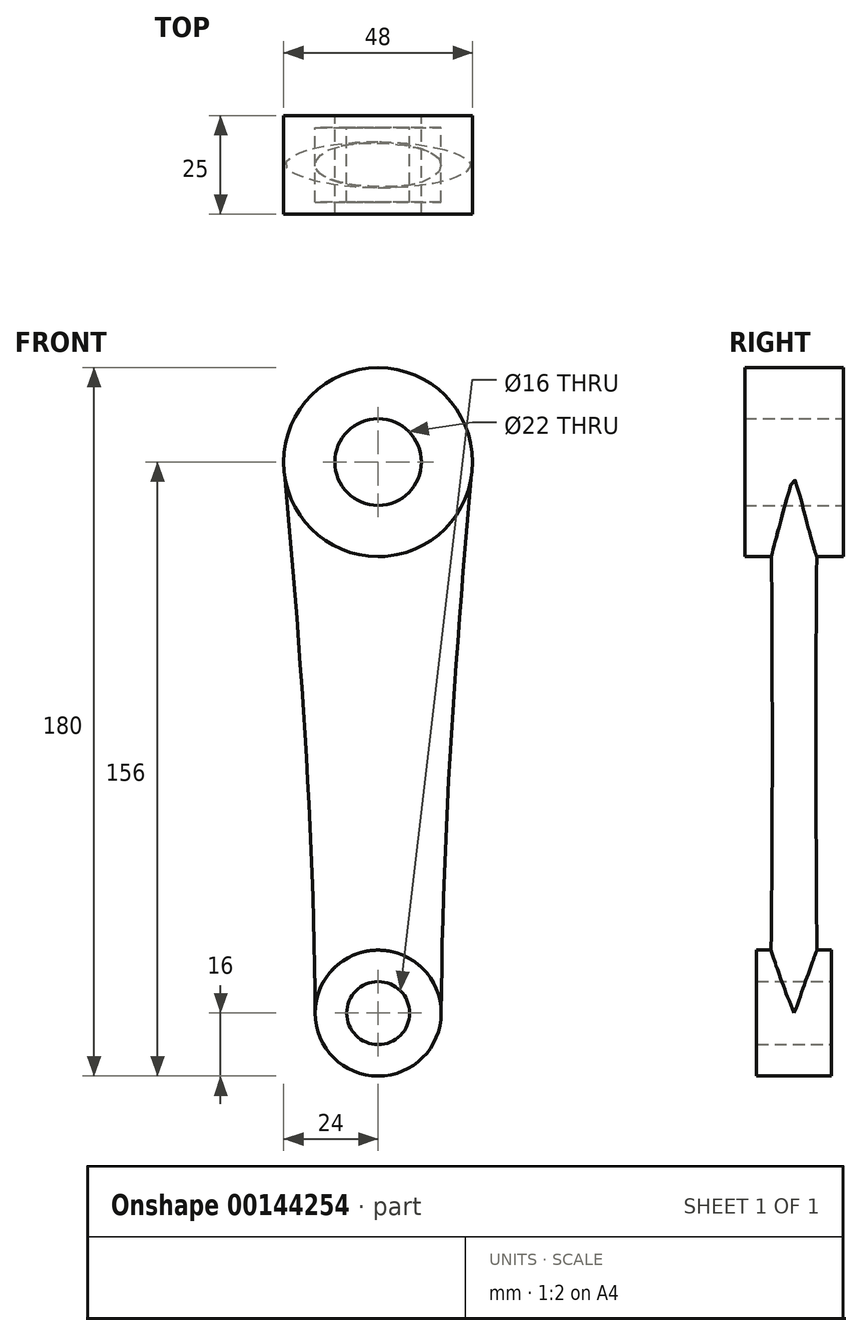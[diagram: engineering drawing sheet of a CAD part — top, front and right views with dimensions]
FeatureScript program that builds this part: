
annotation { "Feature Type Name" : "Feature", "Feature Type Description" : "" }
export const myFeature = defineFeature(function(context is Context, id is Id, definition is map)
    precondition{}
    {
        {
            var Q0;
            Q0=qCreatedBy(makeId("Front.planeOp"),FACE);
            var sketch = newSketch(context, id + "F0", { "sketchPlane" : qUnion([Q0])});
            skCircle(sketch, "E0", {"center": v(0, 140) * mm, "radius": 11 * mm});
            skCircle(sketch, "E1", {"center": v(0, 140) * mm, "radius": 24 * mm});
            skCircle(sketch, "E2", {"center": v(0, 0) * mm, "radius": 8 * mm});
            skCircle(sketch, "E3", {"center": v(0, 0) * mm, "radius": 16 * mm});
            skLineSegment(sketch, "E4", {"start": v(0, 0) * mm, "end": v(0, 140) * mm, "construction": true});
            skSolve(sketch);
        }
        {
            var Q0;
            Q0=makeQuery(id+"F0.imprint","IMPRINT",FACE,{"disambiguationData":[TD([[makeQuery(id+"F0.imprint","IMPRINT",EDGE,{"derivedFrom":sQuery(id+"F0.wireOp",EDGE,"E0")}),-1.0]])]});
            var Q1;
            Q1=makeQuery(id+"F0.imprint","IMPRINT",FACE,{"disambiguationData":[TD([[makeQuery(id+"F0.imprint","IMPRINT",EDGE,{"derivedFrom":sQuery(id+"F0.wireOp",EDGE,"E0")}),1.0]])]});
            extrude(context, id + "F1", {"entities" : qUnion([Q0, Q1]), "endBound" : BoundingType.SYMMETRIC, "depth" : 25 * mm});
        }
        {
            var Q0;
            Q0=qCreatedBy(makeId("Front.planeOp"),FACE);
            var sketch = newSketch(context, id + "F2", { "sketchPlane" : qUnion([Q0])});
            skCircle(sketch, "E5.0", {"center": v(0, 0) * mm, "radius": 16 * mm});
            skCircle(sketch, "E6.0", {"center": v(0, 0) * mm, "radius": 8 * mm});
            skSolve(sketch);
        }
        {
            var Q0;
            Q0 = qSketchRegion(id + "F2", true);
            var Q1;
            Q1=makeQuery(id+"F0.imprint","IMPRINT",FACE,{"disambiguationData":[TD([[makeQuery(id+"F0.imprint","IMPRINT",EDGE,{"derivedFrom":sQuery(id+"F0.wireOp",EDGE,"E2")}),1.0]])]});
            extrude(context, id + "F3", {"entities" : qUnion([Q0, Q1]), "endBound" : BoundingType.SYMMETRIC, "depth" : 19 * mm});
        }
        {
            var Q0;
            Q0=qCreatedBy(makeId("Top.planeOp"),FACE);
            var sketch = newSketch(context, id + "F4", { "sketchPlane" : qUnion([Q0])});
            skEllipse(sketch, "E7", {"center": v(0, 0) * mm, "majorRadius": 16 * mm, "minorRadius": 6 * mm, "majorAxis": v(1, 0)});
            skLineSegment(sketch, "E8.0", {"start": v(16, 9.5) * mm, "end": v(-16, 9.5) * mm, "construction": true});
            skLineSegment(sketch, "E9.0", {"start": v(16, -9.5) * mm, "end": v(-16, -9.5) * mm, "construction": true});
            skLineSegment(sketch, "E10", {"start": v(16, 9.5) * mm, "end": v(16, -9.5) * mm, "construction": true});
            skSolve(sketch);
        }
        {
            var Q0;
            Q0=sQuery(id+"F0.wireOp",VERTEX,"E1.center");
            var Q1;
            Q1=qCreatedBy(makeId("Top.planeOp"),FACE);
            cPlane(context, id + "F5", {"entities" : qUnion([Q0, Q1]), "cplaneType" : CPlaneType.PLANE_POINT, "offset" : 25 * mm, "width" : 150 * mm, "height" : 150 * mm});
        }
        {
            var Q0;
            Q0=qCreatedBy(id+"F5.planeOp",FACE);
            var sketch = newSketch(context, id + "F6", { "sketchPlane" : qUnion([Q0])});
            skEllipse(sketch, "E11", {"center": v(0, 0) * mm, "majorRadius": 24 * mm, "minorRadius": 6 * mm, "majorAxis": v(-1, 0)});
            skLineSegment(sketch, "E12.0", {"start": v(24, 12.5) * mm, "end": v(-24, 12.5) * mm, "construction": true});
            skLineSegment(sketch, "E13.0", {"start": v(24, -12.5) * mm, "end": v(-24, -12.5) * mm, "construction": true});
            skLineSegment(sketch, "E14", {"start": v(24, 12.5) * mm, "end": v(24, -12.5) * mm, "construction": true});
            skSolve(sketch);
        }
        {
            var Q0;
            Q0=makeQuery(id+"F4.imprint","IMPRINT",FACE,{"disambiguationData":[TD([[makeQuery(id+"F4.imprint","IMPRINT",EDGE,{"derivedFrom":sQuery(id+"F4.wireOp",EDGE,"E7")}),1.0]])]});
            var Q1;
            Q1=makeQuery(id+"F6.imprint","IMPRINT",FACE,{"disambiguationData":[TD([[makeQuery(id+"F6.imprint","IMPRINT",EDGE,{"derivedFrom":sQuery(id+"F6.wireOp",EDGE,"E11")}),1.0]])]});
            loft(context, id + "F7", {"operationType" : NewBodyOperationType.ADD, "sheetProfilesArray" : [{ "sheetProfileEntities" : qUnion([Q0]) }, { "sheetProfileEntities" : qUnion([Q1]) }]});
        }
        {
            var Q0;
            Q0=qCreatedBy(makeId("Front.planeOp"),FACE);
            var sketch = newSketch(context, id + "F8", { "sketchPlane" : qUnion([Q0])});
            skCircle(sketch, "E15.0", {"center": v(0, 140) * mm, "radius": 11 * mm});
            skCircle(sketch, "E16.0", {"center": v(0, 0) * mm, "radius": 8 * mm});
            skSolve(sketch);
        }
        {
            var Q0;
            Q0 = qSketchRegion(id + "F8", true);
            extrude(context, id + "F9", {"entities" : qUnion([Q0]), "operationType" : NewBodyOperationType.REMOVE, "depth" : 25 * mm});
        }
        {
            var Q0;
            Q0=qCreatedBy(makeId("Front.planeOp"),FACE);
            var sketch = newSketch(context, id + "F10", { "sketchPlane" : qUnion([Q0])});
            skCircle(sketch, "E17.0", {"center": v(0, 140) * mm, "radius": 11 * mm});
            skCircle(sketch, "E18.0", {"center": v(0, 0) * mm, "radius": 8 * mm});
            skSolve(sketch);
        }
        {
            var Q0;
            Q0 = qSketchRegion(id + "F10", true);
            extrude(context, id + "F11", {"entities" : qUnion([Q0]), "operationType" : NewBodyOperationType.REMOVE, "oppositeDirection" : true, "depth" : 25 * mm});
        }
    });
